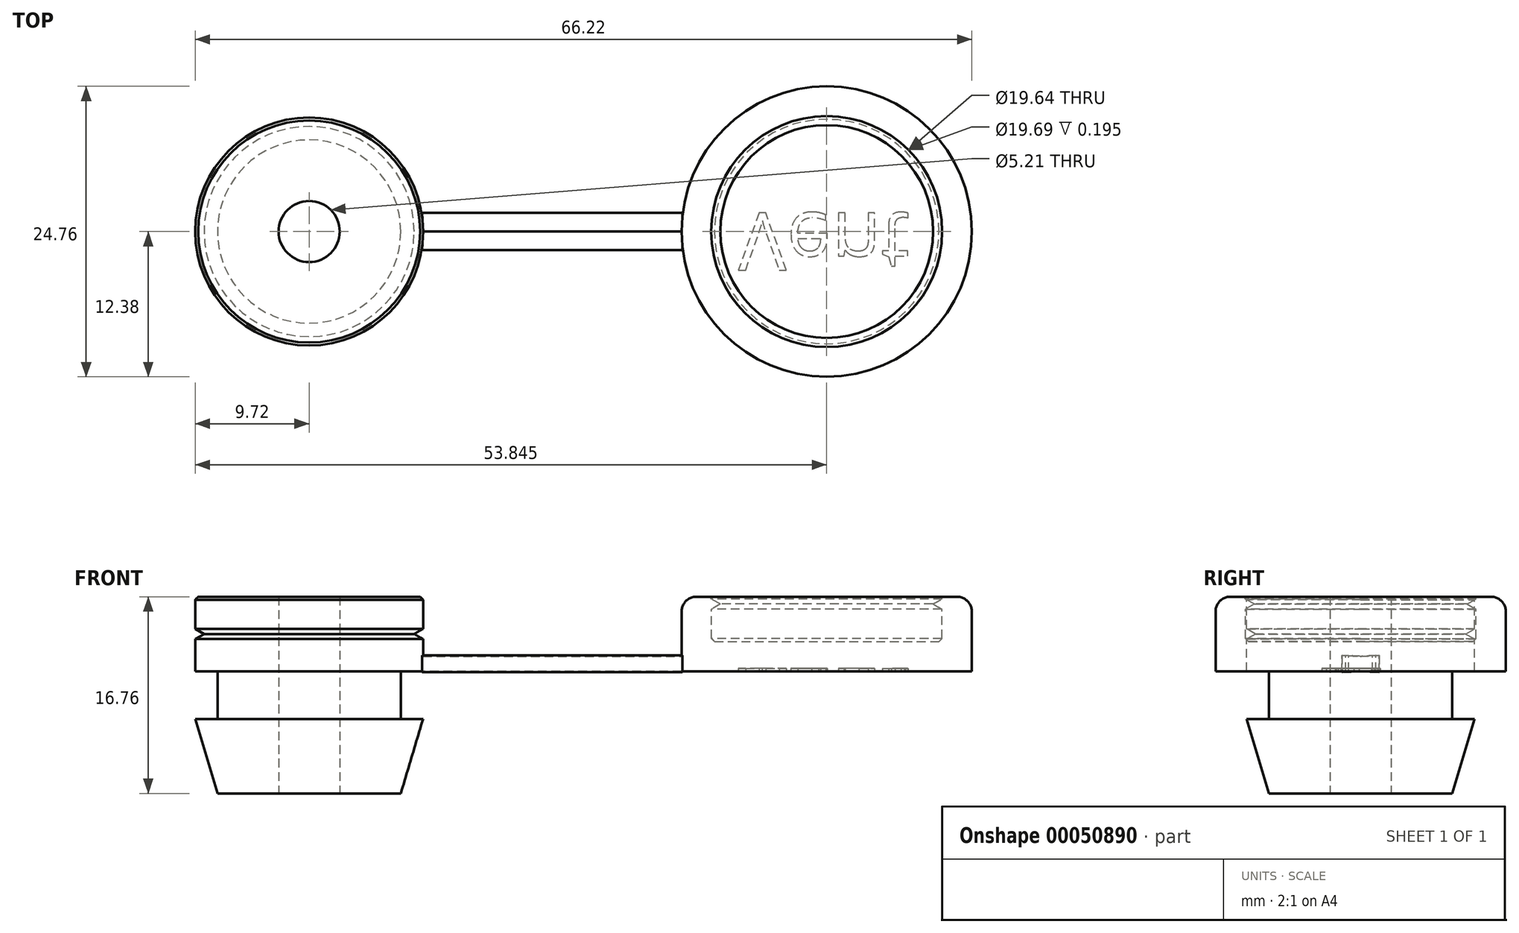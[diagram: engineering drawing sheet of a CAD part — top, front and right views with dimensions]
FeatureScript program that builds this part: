
annotation { "Feature Type Name" : "Feature", "Feature Type Description" : "" }
export const myFeature = defineFeature(function(context is Context, id is Id, definition is map)
    precondition{}
    {
        {
            var Q0;
            Q0=qCreatedBy(makeId("Front.planeOp"),FACE);
            var sketch = newSketch(context, id + "F0", { "sketchPlane" : qUnion([Q0])});
            skLineSegment(sketch, "E0", {"start": v(0, 0) * mm, "end": v(-7.81, 0) * mm});
            skLineSegment(sketch, "E1", {"start": v(-7.81, 0) * mm, "end": v(-9.72, 6.35) * mm});
            skLineSegment(sketch, "E2", {"start": v(-9.72, 6.35) * mm, "end": v(-7.81, 6.35) * mm});
            skLineSegment(sketch, "E3", {"start": v(-7.81, 6.35) * mm, "end": v(-7.81, 10.41) * mm});
            skLineSegment(sketch, "E4", {"start": v(-9.72, 16.76) * mm, "end": v(0, 16.76) * mm});
            skLineSegment(sketch, "E5", {"start": v(0, 16.76) * mm, "end": v(0, 0) * mm});
            skLineSegment(sketch, "E6", {"start": v(-5.2, 16.76) * mm, "end": v(-5.2, 0) * mm, "construction": true});
            skLineSegment(sketch, "E7", {"start": v(-7.81, 10.41) * mm, "end": v(-9.72, 10.41) * mm});
            skLineSegment(sketch, "E8", {"start": v(-10.16, 13.59) * mm, "end": v(0, 13.59) * mm, "construction": true});
            skLineSegment(sketch, "E9", {"start": v(-9.72, 16.76) * mm, "end": v(-9.72, 14.03) * mm});
            skLineSegment(sketch, "E10", {"start": v(-9.72, 14.03) * mm, "end": v(-8.95, 13.59) * mm});
            skLineSegment(sketch, "E11", {"start": v(-8.95, 13.59) * mm, "end": v(-9.72, 13.15) * mm});
            skLineSegment(sketch, "E12", {"start": v(-9.72, 13.15) * mm, "end": v(-9.72, 10.41) * mm});
            skLineSegment(sketch, "E13", {"start": v(-9.72, 14.03) * mm, "end": v(-9.72, 13.15) * mm, "construction": true});
            skLineSegment(sketch, "E14", {"start": v(31.75, 16.76) * mm, "end": v(31.75, 0) * mm, "construction": true});
            skLineSegment(sketch, "E15", {"start": v(-7.81, 10.41) * mm, "end": v(31.75, 10.41) * mm, "construction": true});
            skLineSegment(sketch, "E16", {"start": v(0, 16.76) * mm, "end": v(31.75, 16.76) * mm, "construction": true});
            skLineSegment(sketch, "E17", {"start": v(31.75, 16.76) * mm, "end": v(31.75, 10.41) * mm});
            skLineSegment(sketch, "E18", {"start": v(31.75, 16.76) * mm, "end": v(34.28, 16.76) * mm});
            skLineSegment(sketch, "E19", {"start": v(34.28, 16.76) * mm, "end": v(34.28, 16.57) * mm});
            skLineSegment(sketch, "E20", {"start": v(34.28, 16.57) * mm, "end": v(35.06, 16.15) * mm});
            skLineSegment(sketch, "E21", {"start": v(35.06, 16.15) * mm, "end": v(34.3, 15.69) * mm});
            skLineSegment(sketch, "E22", {"start": v(34.3, 15.69) * mm, "end": v(34.3, 12.95) * mm});
            skLineSegment(sketch, "E23", {"start": v(34.3, 12.95) * mm, "end": v(44.13, 12.95) * mm});
            skLineSegment(sketch, "E24", {"start": v(44.13, 12.95) * mm, "end": v(44.13, 10.41) * mm});
            skLineSegment(sketch, "E25", {"start": v(34.28, 16.57) * mm, "end": v(34.3, 15.69) * mm, "construction": true});
            skLineSegment(sketch, "E26", {"start": v(31.75, 10.41) * mm, "end": v(31.75, 10.41) * mm});
            skLineSegment(sketch, "E27", {"start": v(31.75, 10.41) * mm, "end": v(44.13, 10.41) * mm});
            skLineSegment(sketch, "E28", {"start": v(9.72, 16.76) * mm, "end": v(9.72, 0) * mm, "construction": true});
            skLineSegment(sketch, "E29", {"start": v(9.72, 11.68) * mm, "end": v(9.72, 10.41) * mm});
            skLineSegment(sketch, "E30", {"start": v(9.72, 10.41) * mm, "end": v(31.75, 10.41) * mm});
            skLineSegment(sketch, "E31", {"start": v(9.72, 11.68) * mm, "end": v(31.75, 11.68) * mm});
            skPoint(sketch, "E32.orphan", {"position": v(31.75, 11.68) * mm});
            skSolve(sketch);
        }
        {
            var Q0;
            {var subQ1=sQuery(id+"F0.wireOp",EDGE,"E0");Q0=makeQuery(id+"F0.imprint","IMPRINT",FACE,{"disambiguationData":[TD([[makeQuery(id+"F0.imprint","IMPRINT",EDGE,{"derivedFrom":subQ1}),-1.0]])]});}
            var Q1;
            Q1=sQuery(id+"F0.wireOp",EDGE,"E5");
            revolve(context, id + "F1", {"entities" : qUnion([Q0]), "axis" : qUnion([Q1]), "revolveType" : RevolveType.FULL});
        }
        {
            var Q0;
            {var subQ0=sQuery(id+"F0.wireOp",EDGE,"E18");Q0=makeQuery(id+"F0.imprint","IMPRINT",FACE,{"disambiguationData":[TD([[makeQuery(id+"F0.imprint","IMPRINT",EDGE,{"derivedFrom":subQ0}),-1.0]])]});}
            var Q1;
            {var subQ5=sQuery(id+"F0.wireOp",EDGE,"851ac59e-3225-4497-8e2e-3891a598f51d");Q1=makeQuery(id+"F0.imprint","IMPRINT",FACE,{"disambiguationData":[TD([[makeQuery(id+"F0.imprint","IMPRINT",EDGE,{"derivedFrom":subQ5}),1.0]])]});}
            var Q2;
            Q2=sQuery(id+"F0.wireOp",EDGE,"E24");
            revolve(context, id + "F2", {"operationType" : NewBodyOperationType.ADD, "entities" : qUnion([Q0, Q1]), "axis" : qUnion([Q2]), "revolveType" : RevolveType.FULL});
        }
        {
            var Q0;
            {var subQ5=sQuery(id+"F0.wireOp",EDGE,"E29");Q0=makeQuery(id+"F0.imprint","IMPRINT",FACE,{"disambiguationData":[TD([[makeQuery(id+"F0.imprint","IMPRINT",EDGE,{"derivedFrom":subQ5}),1.0]])]});}
            extrude(context, id + "F3", {"entities" : qUnion([Q0]), "operationType" : NewBodyOperationType.ADD, "endBound" : BoundingType.SYMMETRIC, "depth" : 3.17 * mm, "hasDraft" : true, "draftAngle" : 3 * degree});
        }
        {
            var Q0;
            Q0=makeQuery(id+"F1.opRevolve","SWEPT_EDGE",EDGE,{"disambiguationData":[OSD([sQuery(id+"F0.wireOp",EDGE,"E4"),sQuery(id+"F0.wireOp",EDGE,"E9")])]});
            var Q1;
            Q1=makeQuery(id+"F2.opRevolve","SWEPT_EDGE",EDGE,{"disambiguationData":[OSD([sQuery(id+"F0.wireOp",EDGE,"E22"),sQuery(id+"F0.wireOp",EDGE,"E23")])]});
            chamfer(context, id + "F4", {"entities" : qUnion([Q0, Q1]), "width" : 0.25 * mm, "tangentPropagation" : true});
        }
        {
            var Q0;
            Q0=makeQuery(id+"F2.opRevolve","SWEPT_EDGE",EDGE,{"disambiguationData":[OSD([sQuery(id+"F0.wireOp",EDGE,"E17"),sQuery(id+"F0.wireOp",EDGE,"E18")])]});
            fillet(context, id + "F5", {"entities" : qUnion([Q0]), "radius" : 1.27 * mm, "tangentPropagation" : true, "allowEdgeOverflow" : false});
        }
        {
            var Q0;
            Q0=makeQuery(id+"F1.opRevolve","SWEPT_FACE",FACE,{"disambiguationData":[OSD([sQuery(id+"F0.wireOp",EDGE,"E0")])]});
            var sketch = newSketch(context, id + "F6", { "sketchPlane" : qUnion([Q0])});
            skCircle(sketch, "E33", {"center": v(0, 0) * mm, "radius": 2.6 * mm});
            skSolve(sketch);
        }
        {
            var Q0;
            Q0=makeQuery(id+"F6.imprint","IMPRINT",FACE,{"disambiguationData":[TD([[makeQuery(id+"F6.imprint","IMPRINT",EDGE,{"derivedFrom":sQuery(id+"F6.wireOp",EDGE,"E33")}),1.0]])]});
            var Q1;
            Q1=sQuery(id+"F6.wireOp",EDGE,"E33");
            extrude(context, id + "F7", {"entities" : qUnion([Q0]), "operationType" : NewBodyOperationType.REMOVE, "surfaceEntities" : qUnion([Q1]), "endBound" : BoundingType.THROUGH_ALL, "oppositeDirection" : true, "depth" : 25.4 * mm});
        }
        {
            var Q0;
            Q0=makeQuery(id+"F2.opRevolve","SWEPT_FACE",FACE,{"disambiguationData":[OSD([sQuery(id+"F0.wireOp",EDGE,"E27")])]});
            var sketch = newSketch(context, id + "F8", { "sketchPlane" : qUnion([Q0])});
            skText(sketch, "E34", { "text": "Vent", "fontName": "OpenSans-Regular.ttf"});
            const initialGuessF8  = {"E34": [0.0366, -0.0016, 1, 0, 0.00495]};
            skSetInitialGuess(sketch, initialGuessF8);
            skSolve(sketch);
        }
        {
            var Q0;
            Q0 = qSketchRegion(id + "F8", true);
            extrude(context, id + "F9", {"entities" : qUnion([Q0]), "operationType" : NewBodyOperationType.REMOVE, "oppositeDirection" : true, "depth" : 0.25 * mm});
        }
    });
